# Revit family: VEGA
name_source: partatom
category: Lighting Fixtures
units: mm (PartAtom-declared; Revit-internal decimal feet)

## family parameters
Always vertical = Yes
Cut with Voids When Loaded = No
Light Source = Yes
Maintain Annotation Orientation = No
OmniClass Number = 23.80.70.00
OmniClass Title = Lighting
Part Type = Normal
Room Calculation Point = No
Round Connector Dimension = Use Diameter
Shared = No
Work Plane-Based = No

## types (1)
- VEGA-18W-3000K-15X30°
    CRI = 70
    Color Filter = 16777215
    Default Elevation = 0' - 0"
    Dimming Lamp Color Temperature Shift = <None>
    IP Rating = 66
    Input Voltage = 24V DC
    Lamp = LED
    Load Classification = Lighting
    Manufacturer = Above All Lighting
    Model = VEGA-1830-24V-15X30
    Photometric Web File = VEGA-18W-3000K-15DX30D.ies
    Power Factor = 0.9
    Tilt Angle = 90.00°
    URL = https://www.abovealllighting.com
    Wattage Comments = 18W

## geometry (parser evidence)
native form markers: Sweep x3
no freeform markers — native parametric forms only
